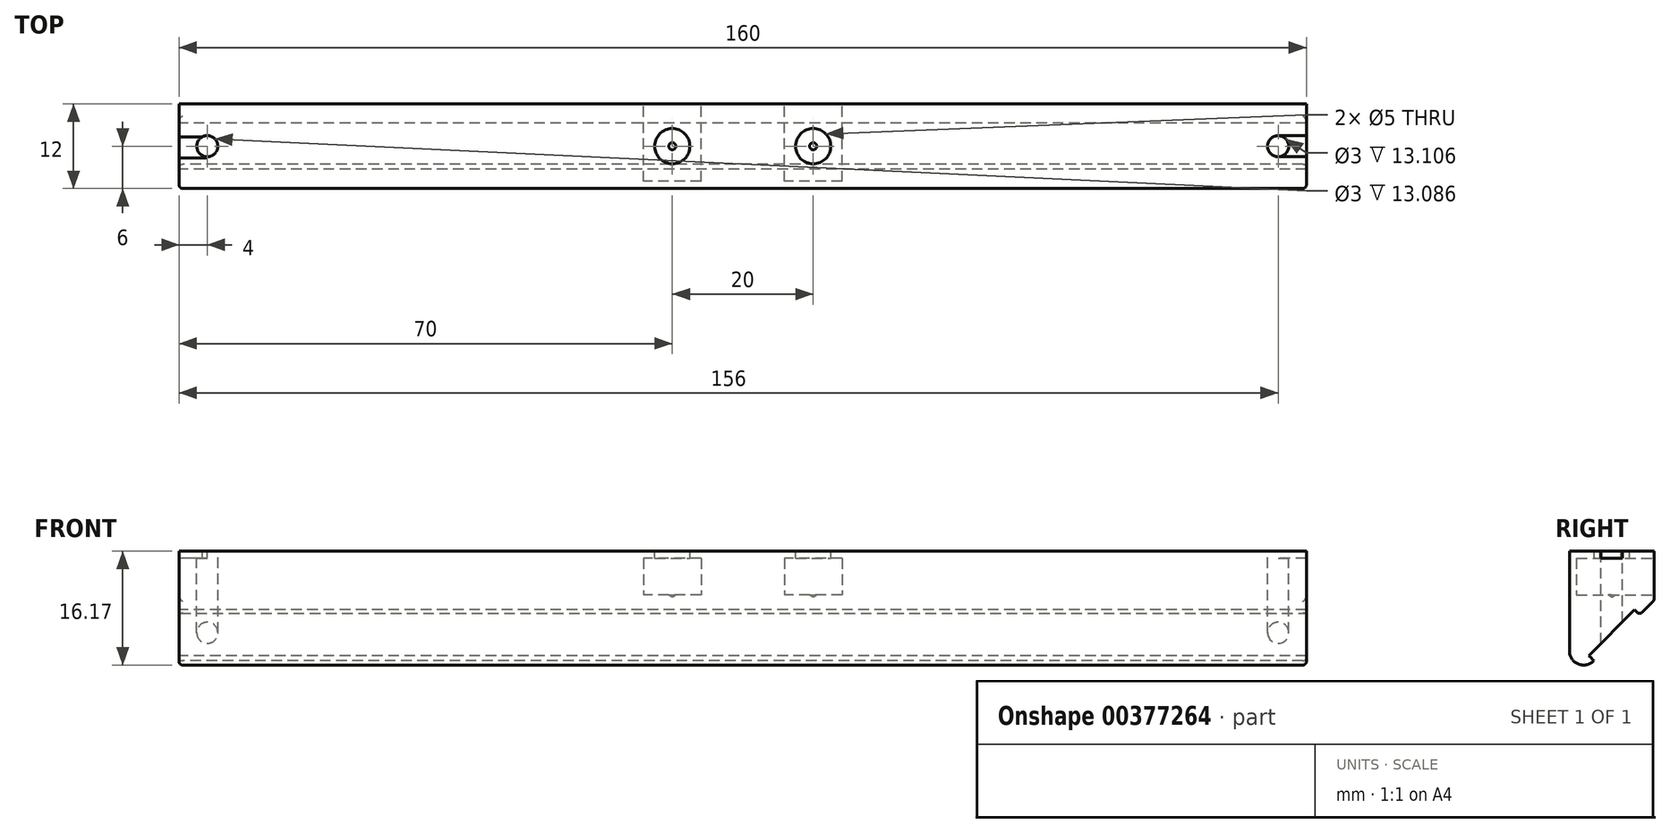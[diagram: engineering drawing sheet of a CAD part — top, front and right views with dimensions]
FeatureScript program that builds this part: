
annotation { "Feature Type Name" : "Feature", "Feature Type Description" : "" }
export const myFeature = defineFeature(function(context is Context, id is Id, definition is map)
    precondition{}
    {
        {
            var Q0;
            Q0=qCreatedBy(makeId("Right.planeOp"),FACE);
            var sketch = newSketch(context, id + "F0", { "sketchPlane" : qUnion([Q0])});
            skLineSegment(sketch, "E0", {"start": v(12, -7) * mm, "end": v(9.96, -9.04) * mm});
            skLineSegment(sketch, "E1", {"start": v(0, -19) * mm, "end": v(0, -6.5) * mm});
            skLineSegment(sketch, "E2", {"start": v(3.45, -15.55) * mm, "end": v(2.75, -14.84) * mm});
            skLineSegment(sketch, "E3", {"start": v(2.75, -14.84) * mm, "end": v(9.25, -8.33) * mm});
            skLineSegment(sketch, "E4", {"start": v(9.25, -8.33) * mm, "end": v(9.96, -9.04) * mm});
            skLineSegment(sketch, "E5.trimOffspring", {"start": v(3.45, -15.55) * mm, "end": v(0, -19) * mm});
            skPoint(sketch, "E6", {"position": v(6, -11.59) * mm});
            skLineSegment(sketch, "E7.trimOffspring", {"start": v(12, -7) * mm, "end": v(12, -7) * mm});
            skLineSegment(sketch, "E8", {"start": v(0, 0) * mm, "end": v(0, -6.5) * mm});
            skLineSegment(sketch, "E9", {"start": v(12, -7) * mm, "end": v(0, -19) * mm, "construction": true});
            skLineSegment(sketch, "E10", {"start": v(12, -7) * mm, "end": v(12, 0) * mm});
            skLineSegment(sketch, "E11", {"start": v(12, 0) * mm, "end": v(0, 0) * mm});
            skPoint(sketch, "E12", {"position": v(6, 0) * mm});
            skPoint(sketch, "E13", {"position": v(0, 0) * mm});
            skLineSegment(sketch, "E14", {"start": v(6, 0) * mm, "end": v(6, -20.82) * mm, "construction": true});
            skSolve(sketch);
        }
        {
            var Q0;
            Q0=qSketchRegion(id+"F0",true);
            extrude(context, id + "F1", {"entities" : qUnion([Q0]), "depth" : 160 * mm});
        }
        {
            var Q0;
            Q0=makeQuery(id+"F1.opExtrude","SWEPT_FACE",FACE,{"disambiguationData":[OSD([sQuery(id+"F0.wireOp",EDGE,"E11")])]});
            var sketch = newSketch(context, id + "F2", { "sketchPlane" : qUnion([Q0])});
            skLineSegment(sketch, "E15", {"start": v(-12.3, 6) * mm, "end": v(165.16, 6) * mm, "construction": true});
            skPoint(sketch, "E16", {"position": v(70, 6) * mm});
            skLineSegment(sketch, "E17", {"start": v(80, 11.64) * mm, "end": v(80, -1.6) * mm, "construction": true});
            skPoint(sketch, "E18", {"position": v(90, 6) * mm});
            skSolve(sketch);
        }
        {
            var Q0;
            Q0=sQuery(id+"F2.wireOp",VERTEX,"E18");
            var Q1;
            Q1=sQuery(id+"F2.wireOp",VERTEX,"E16");
            var Q2;
            Q2=makeQuery(id+"F1.opExtrude","SWEPT_BODY",BODY,{"disambiguationData":[OSD([sQuery(id+"F0.wireOp",EDGE,"Svc9P5s6-Hczd-MqYI-ylew-wP2RNLbnXJCC"),sQuery(id+"F0.wireOp",EDGE,"11svOsqp-XJxs-fWXj-VL2F-PPj4Q2sBWO4S"),sQuery(id+"F0.wireOp",EDGE,"E0"),sQuery(id+"F0.wireOp",EDGE,"E1"),sQuery(id+"F0.wireOp",EDGE,"weEhJJmv-kteP-NT3w-WIeD-G58RNwuArdjz"),sQuery(id+"F0.wireOp",EDGE,"ys592Dv6-fJ9H-k703-X8Kf-owWBb4tYEX4s"),sQuery(id+"F0.wireOp",EDGE,"HZxZGGoi-akEo-FQfd-lKEf-4JcA7kei3745"),sQuery(id+"F0.wireOp",EDGE,"GfhF2z7a-uS4p-iOlK-2Cc6-JkVw7Kw1EZmj"),sQuery(id+"F0.wireOp",EDGE,"E2"),sQuery(id+"F0.wireOp",EDGE,"E3"),sQuery(id+"F0.wireOp",EDGE,"E4"),sQuery(id+"F0.wireOp",EDGE,"E5.trimOffspring")])]});
            hole(context, id + "F3", {"style" : HoleStyle.SIMPLE, "endStyle" : HoleEndStyle.BLIND, "holeDiameter" : 5 * mm, "holeDepth" : 5 * mm, "locations" : qUnion([Q0, Q1]), "scope" : qUnion([Q2])});
        }
        {
            var Q0;
            Q0=makeQuery(id+"F1.opExtrude","SWEPT_FACE",FACE,{"disambiguationData":[OSD([sQuery(id+"F0.wireOp",EDGE,"E10")])]});
            var sketch = newSketch(context, id + "F4", { "sketchPlane" : qUnion([Q0])});
            skLineSegment(sketch, "E19.bottom", {"start": v(-94.1, -1) * mm, "end": v(-85.9, -1) * mm});
            skLineSegment(sketch, "E19.top", {"start": v(-94.1, -6.2) * mm, "end": v(-85.9, -6.2) * mm});
            skLineSegment(sketch, "E19.left", {"start": v(-94.1, -1) * mm, "end": v(-94.1, -6.2) * mm});
            skLineSegment(sketch, "E19.right", {"start": v(-85.9, -1) * mm, "end": v(-85.9, -6.2) * mm});
            skLineSegment(sketch, "E20", {"start": v(-80, 21.81) * mm, "end": v(-80, -19.64) * mm, "construction": true});
            skLineSegment(sketch, "E21.bottom", {"start": v(-74.1, -1) * mm, "end": v(-65.9, -1) * mm});
            skLineSegment(sketch, "E21.top", {"start": v(-74.1, -6.2) * mm, "end": v(-65.9, -6.2) * mm});
            skLineSegment(sketch, "E21.left", {"start": v(-74.1, -1) * mm, "end": v(-74.1, -6.2) * mm});
            skLineSegment(sketch, "E21.right", {"start": v(-65.9, -1) * mm, "end": v(-65.9, -6.2) * mm});
            skLineSegment(sketch, "E22", {"start": v(-70, 25.04) * mm, "end": v(-70, -21.63) * mm, "construction": true});
            skLineSegment(sketch, "E23", {"start": v(-100.88, -1) * mm, "end": v(-57.33, -1) * mm, "construction": true});
            skSolve(sketch);
        }
        {
            var Q0;
            Q0=qSketchRegion(id+"F4",true);
            extrude(context, id + "F5", {"entities" : qUnion([Q0]), "operationType" : NewBodyOperationType.REMOVE, "oppositeDirection" : true, "depth" : 11 * mm});
        }
        {
            var Q0;
            Q0=qCreatedBy(makeId("Top.planeOp"),FACE);
            var sketch = newSketch(context, id + "F6", { "sketchPlane" : qUnion([Q0])});
            skPoint(sketch, "E24", {"position": v(4, 6) * mm});
            skPoint(sketch, "E25", {"position": v(156, 6) * mm});
            skLineSegment(sketch, "E26.bottom", {"start": v(160, 4.5) * mm, "end": v(156, 4.5) * mm});
            skLineSegment(sketch, "E26.top", {"start": v(160, 7.5) * mm, "end": v(156, 7.5) * mm});
            skLineSegment(sketch, "E26.left", {"start": v(160, 4.5) * mm, "end": v(160, 7.5) * mm});
            skLineSegment(sketch, "E26.right", {"start": v(156, 4.5) * mm, "end": v(156, 7.5) * mm});
            skLineSegment(sketch, "E27.bottom", {"start": v(4, 4.32) * mm, "end": v(0, 4.32) * mm});
            skLineSegment(sketch, "E27.top", {"start": v(4, 7.32) * mm, "end": v(0, 7.32) * mm});
            skLineSegment(sketch, "E27.left", {"start": v(4, 4.32) * mm, "end": v(4, 7.32) * mm});
            skLineSegment(sketch, "E27.right", {"start": v(0, 4.32) * mm, "end": v(0, 7.32) * mm});
            skSolve(sketch);
        }
        {
            var Q0;
            Q0=sQuery(id+"F6.wireOp",VERTEX,"E24");
            var Q1;
            Q1=sQuery(id+"F6.wireOp",VERTEX,"E25");
            var Q2;
            Q2=makeQuery(id+"F1.opExtrude","SWEPT_BODY",BODY,{"disambiguationData":[OSD([sQuery(id+"F0.wireOp",EDGE,"Svc9P5s6-Hczd-MqYI-ylew-wP2RNLbnXJCC"),sQuery(id+"F0.wireOp",EDGE,"11svOsqp-XJxs-fWXj-VL2F-PPj4Q2sBWO4S"),sQuery(id+"F0.wireOp",EDGE,"E0"),sQuery(id+"F0.wireOp",EDGE,"E1"),sQuery(id+"F0.wireOp",EDGE,"E2"),sQuery(id+"F0.wireOp",EDGE,"E3"),sQuery(id+"F0.wireOp",EDGE,"E4"),sQuery(id+"F0.wireOp",EDGE,"E5.trimOffspring"),sQuery(id+"F0.wireOp",EDGE,"TSNPTYKX-uX33-WEXj-Thn8-xUD6K22BhvHx"),sQuery(id+"F0.wireOp",EDGE,"p8NVuYJH-O6XB-8Aly-g5sa-1vzSItd6Wojr"),sQuery(id+"F0.wireOp",EDGE,"KqqUjev8-Yawy-KLgQ-uRkK-6fjQIsS6UaKo"),sQuery(id+"F0.wireOp",EDGE,"E7.trimOffspring"),sQuery(id+"F0.wireOp",EDGE,"E8")])]});
            hole(context, id + "F7", {"style" : HoleStyle.SIMPLE, "endStyle" : HoleEndStyle.THROUGH, "holeDiameter" : 3 * mm, "locations" : qUnion([Q0, Q1]), "scope" : qUnion([Q2]), "isTappedThrough" : true});
        }
        {
            var Q0;
            Q0=qSketchRegion(id+"F6",true);
            extrude(context, id + "F8", {"entities" : qUnion([Q0]), "operationType" : NewBodyOperationType.REMOVE, "oppositeDirection" : true, "depth" : 1 * mm});
        }
        {
            var Q0;
            Q0=makeQuery(id+"F1.opExtrude","SWEPT_EDGE",EDGE,{"disambiguationData":[OSD([sQuery(id+"F0.wireOp",EDGE,"E1"),sQuery(id+"F0.wireOp",EDGE,"E5.trimOffspring")])]});
            fillet(context, id + "F9", {"entities" : qUnion([Q0]), "radius" : 2 * mm, "tangentPropagation" : true, "allowEdgeOverflow" : false});
        }
        {
            var Q0;
            Q0=makeQuery(id+"F1.opExtrude","SWEPT_FACE",FACE,{"disambiguationData":[OSD([sQuery(id+"F0.wireOp",EDGE,"11svOsqp-XJxs-fWXj-VL2F-PPj4Q2sBWO4S")])]});
            var Q1;
            Q1=makeQuery(id+"F1.opExtrude","SWEPT_FACE",FACE,{"disambiguationData":[OSD([sQuery(id+"F0.wireOp",EDGE,"Svc9P5s6-Hczd-MqYI-ylew-wP2RNLbnXJCC")])]});
            var Q2;
            Q2=makeQuery(id+"F1.opExtrude","SWEPT_EDGE",EDGE,{"disambiguationData":[OSD([sQuery(id+"F0.wireOp",EDGE,"E0"),sQuery(id+"F0.wireOp",EDGE,"E7.trimOffspring")])]});
            var Q3;
            Q3=makeQuery(id+"F1.opExtrude","SWEPT_EDGE",EDGE,{"disambiguationData":[OSD([sQuery(id+"F0.wireOp",EDGE,"KqqUjev8-Yawy-KLgQ-uRkK-6fjQIsS6UaKo"),sQuery(id+"F0.wireOp",EDGE,"E7.trimOffspring")])]});
            var Q4;
            Q4=makeQuery(id+"F1.opExtrude","CAP_EDGE",EDGE,{"disambiguationData":[OSD([sQuery(id+"F0.wireOp",EDGE,"E0")])],"isStart":false});
            var Q5;
            Q5=makeQuery(id+"F1.opExtrude","CAP_EDGE",EDGE,{"disambiguationData":[OSD([sQuery(id+"F0.wireOp",EDGE,"E0")])],"isStart":true});
            var Q6;
            Q6=makeQuery(id+"F1.opExtrude","CAP_EDGE",EDGE,{"disambiguationData":[OSD([sQuery(id+"F0.wireOp",EDGE,"E7.trimOffspring")])],"isStart":true});
            var Q7;
            Q7=makeQuery(id+"F1.opExtrude","CAP_EDGE",EDGE,{"disambiguationData":[OSD([sQuery(id+"F0.wireOp",EDGE,"E7.trimOffspring")])],"isStart":false});
            var Q8;
            Q8=makeQuery(id+"F1.opExtrude","CAP_EDGE",EDGE,{"disambiguationData":[OSD([sQuery(id+"F0.wireOp",EDGE,"E5.trimOffspring")])],"isStart":false});
            var Q9;
            Q9=makeQuery(id+"F1.opExtrude","CAP_EDGE",EDGE,{"disambiguationData":[OSD([sQuery(id+"F0.wireOp",EDGE,"E5.trimOffspring")])],"isStart":true});
            fillet(context, id + "F10", {"entities" : qUnion([Q0, Q1, Q2, Q3, Q4, Q5, Q6, Q7, Q8, Q9]), "radius" : 0.5 * mm, "tangentPropagation" : true, "allowEdgeOverflow" : false});
        }
    });
